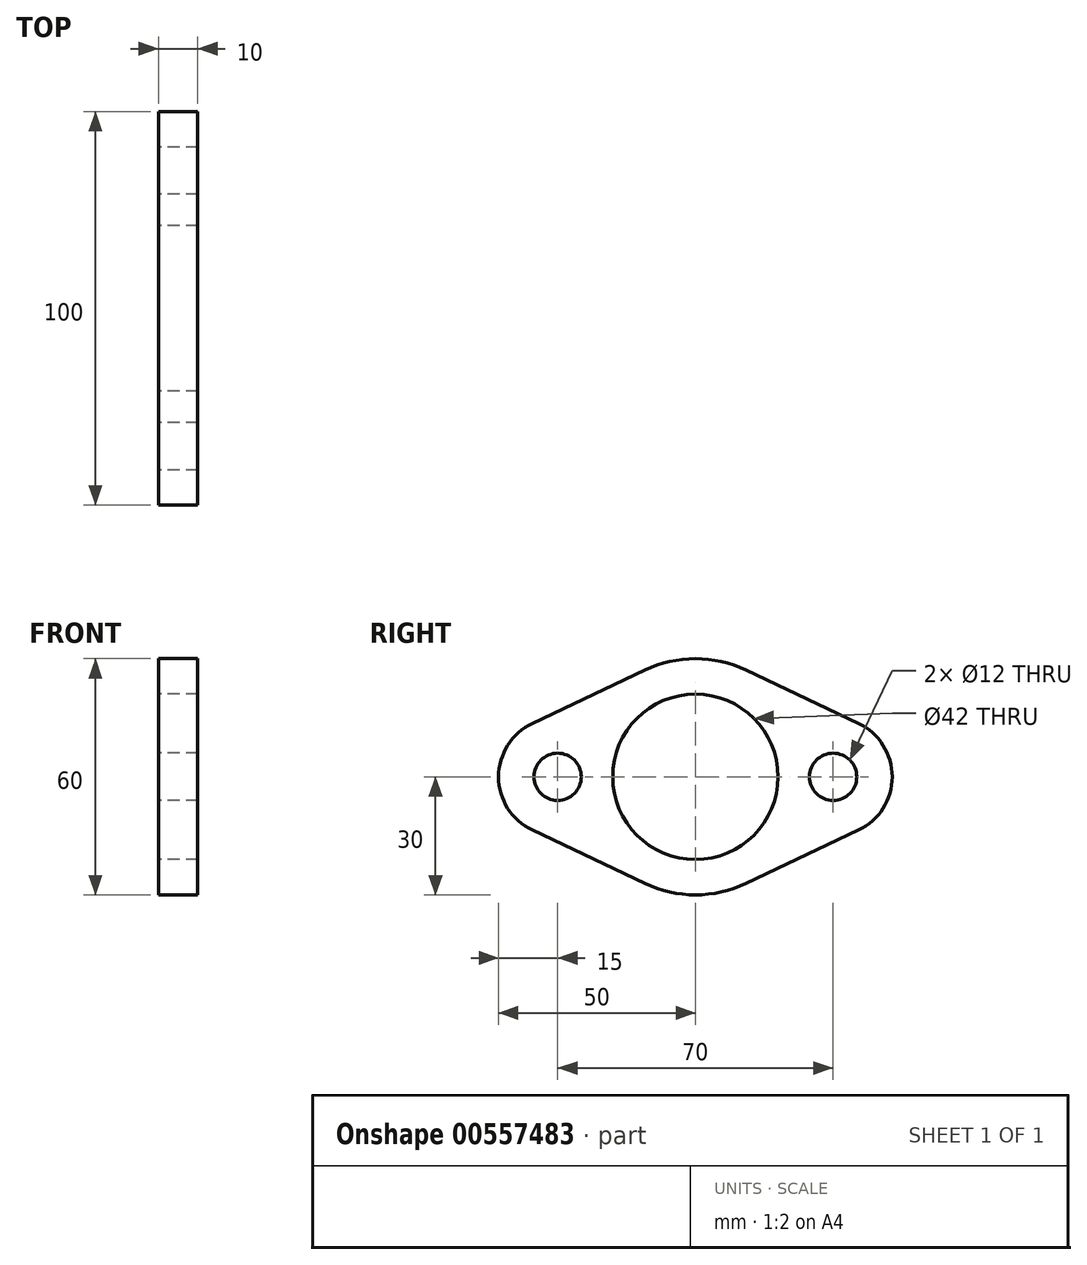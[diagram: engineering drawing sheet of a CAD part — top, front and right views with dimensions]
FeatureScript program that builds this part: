
annotation { "Feature Type Name" : "Feature", "Feature Type Description" : "" }
export const myFeature = defineFeature(function(context is Context, id is Id, definition is map)
    precondition{}
    {
        {
            var Q0;
            Q0=qCreatedBy(makeId("Right.planeOp"),FACE);
            var sketch = newSketch(context, id + "F0", { "sketchPlane" : qUnion([Q0])});
            skCircle(sketch, "E0", {"center": v(0, 0) * mm, "radius": 21 * mm});
            skArc(sketch, "E1", {"start": v(-12.86, -27.1) * mm, "mid": v(0, -30) * mm, "end": v(12.86, -27.1) * mm});
            skCircle(sketch, "E2", {"center": v(35, 0) * mm, "radius": 6 * mm});
            skCircle(sketch, "E3", {"center": v(-35, 0) * mm, "radius": 6 * mm});
            skArc(sketch, "E4", {"start": v(-41.43, 13.55) * mm, "mid": v(-50, 0) * mm, "end": v(-41.43, -13.55) * mm});
            skArc(sketch, "E5", {"start": v(41.43, -13.55) * mm, "mid": v(50, 0) * mm, "end": v(41.43, 13.55) * mm});
            skLineSegment(sketch, "E6", {"start": v(-41.43, 13.55) * mm, "end": v(-12.86, 27.1) * mm});
            skLineSegment(sketch, "E7", {"start": v(-41.43, -13.55) * mm, "end": v(-12.86, -27.1) * mm});
            skLineSegment(sketch, "E8", {"start": v(12.86, 27.1) * mm, "end": v(41.43, 13.55) * mm});
            skLineSegment(sketch, "E9", {"start": v(12.86, -27.1) * mm, "end": v(41.43, -13.55) * mm});
            skArc(sketch, "E10.trimOffspring", {"start": v(12.86, 27.1) * mm, "mid": v(0, 30) * mm, "end": v(-12.86, 27.1) * mm});
            skSolve(sketch);
        }
        {
            var Q0;
            Q0=makeQuery(id+"F0.imprint","IMPRINT",FACE,{"disambiguationData":[TD([[makeQuery(id+"F0.imprint","IMPRINT",EDGE,{"derivedFrom":sQuery(id+"F0.wireOp",EDGE,"E0")}),-1.0]])]});
            extrude(context, id + "F1", {"entities" : qUnion([Q0]), "depth" : 10 * mm, "offsetDistance" : 25 * mm});
        }
    });
